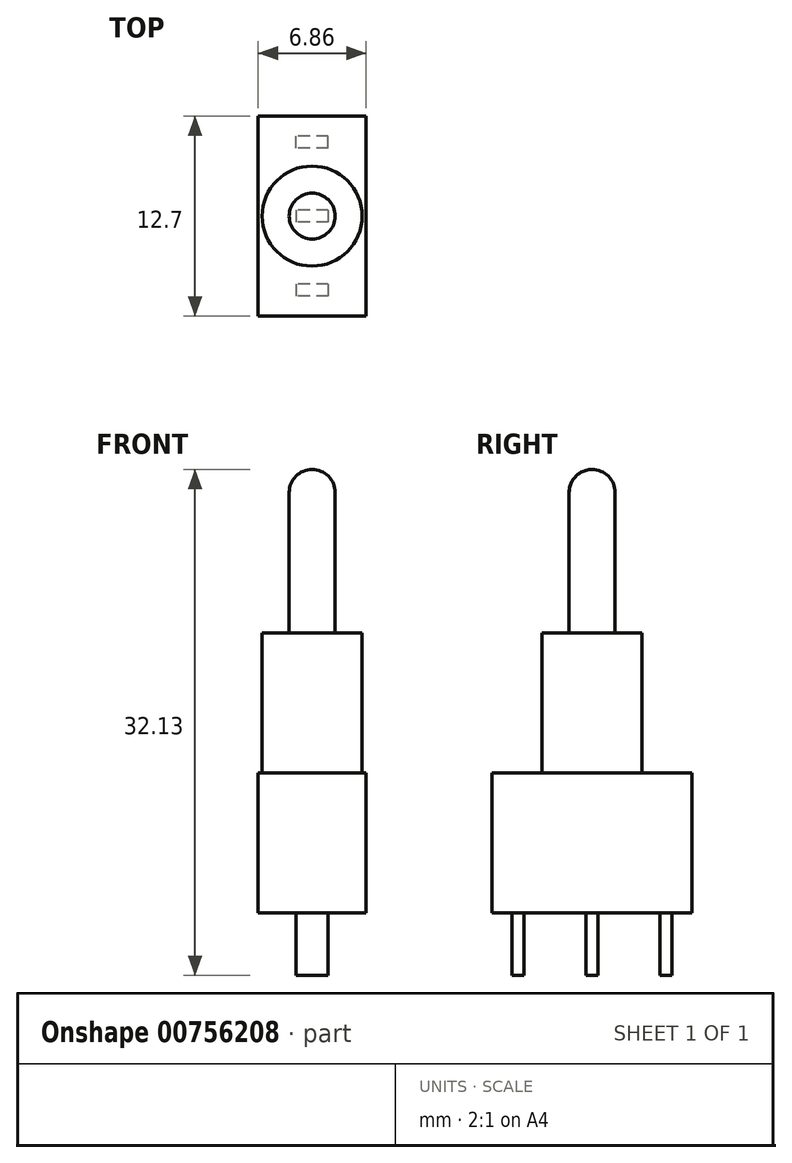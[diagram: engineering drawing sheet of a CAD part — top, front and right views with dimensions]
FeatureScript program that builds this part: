
annotation { "Feature Type Name" : "Feature", "Feature Type Description" : "" }
export const myFeature = defineFeature(function(context is Context, id is Id, definition is map)
    precondition{}
    {
        {
            var Q0;
            Q0=qCreatedBy(makeId("Top.planeOp"),FACE);
            var sketch = newSketch(context, id + "F0", { "sketchPlane" : qUnion([Q0])});
            skLineSegment(sketch, "E0.bottom", {"start": v(-3.43, 6.35) * mm, "end": v(3.43, 6.35) * mm});
            skLineSegment(sketch, "E0.top", {"start": v(-3.43, -6.35) * mm, "end": v(3.43, -6.35) * mm});
            skLineSegment(sketch, "E0.left", {"start": v(-3.43, 6.35) * mm, "end": v(-3.43, -6.35) * mm});
            skLineSegment(sketch, "E0.right", {"start": v(3.43, 6.35) * mm, "end": v(3.43, -6.35) * mm});
            skPoint(sketch, "E0.middle", {"position": v(0, 0) * mm});
            skSolve(sketch);
        }
        {
            var Q0;
            Q0 = qSketchRegion(id + "F0", true);
            extrude(context, id + "F1", {"entities" : qUnion([Q0]), "endBound" : BoundingType.SYMMETRIC, "depth" : 8.9 * mm, "offsetDistance" : 25 * mm});
        }
        {
            var Q0;
            Q0=makeQuery(id+"F1.opExtrude","CAP_FACE",FACE,{"disambiguationData":[OSD([sQuery(id+"F0.wireOp",EDGE,"E0.bottom"),sQuery(id+"F0.wireOp",EDGE,"E0.top"),sQuery(id+"F0.wireOp",EDGE,"E0.left"),sQuery(id+"F0.wireOp",EDGE,"E0.right")])],"isStart":false});
            var sketch = newSketch(context, id + "F2", { "sketchPlane" : qUnion([Q0])});
            skCircle(sketch, "E1", {"center": v(0, 0) * mm, "radius": 3.18 * mm});
            skSolve(sketch);
        }
        {
            var Q0;
            Q0 = qSketchRegion(id + "F2", true);
            extrude(context, id + "F3", {"entities" : qUnion([Q0]), "operationType" : NewBodyOperationType.ADD, "depth" : 8.9 * mm, "offsetDistance" : 25 * mm});
        }
        {
            var Q0;
            Q0=makeQuery(id+"F1.opExtrude","CAP_FACE",FACE,{"disambiguationData":[OSD([sQuery(id+"F0.wireOp",EDGE,"E0.bottom"),sQuery(id+"F0.wireOp",EDGE,"E0.top"),sQuery(id+"F0.wireOp",EDGE,"E0.left"),sQuery(id+"F0.wireOp",EDGE,"E0.right")])],"isStart":true});
            var sketch = newSketch(context, id + "F4", { "sketchPlane" : qUnion([Q0])});
            skLineSegment(sketch, "E2.bottom", {"start": v(1.01, -0.37) * mm, "end": v(-1.01, -0.38) * mm});
            skLineSegment(sketch, "E2.top", {"start": v(1.01, 0.38) * mm, "end": v(-1.01, 0.37) * mm});
            skLineSegment(sketch, "E2.left", {"start": v(1.01, -0.37) * mm, "end": v(1.01, 0.38) * mm});
            skLineSegment(sketch, "E2.right", {"start": v(-1.01, -0.38) * mm, "end": v(-1.01, 0.37) * mm});
            skPoint(sketch, "E2.middle", {"position": v(0, 0) * mm});
            skLineSegment(sketch, "E3.bottom", {"start": v(1.01, -4.32) * mm, "end": v(-1.01, -4.32) * mm});
            skLineSegment(sketch, "E3.top", {"start": v(1.01, -5.08) * mm, "end": v(-1.01, -5.08) * mm});
            skLineSegment(sketch, "E3.left", {"start": v(1.01, -4.32) * mm, "end": v(1.01, -5.08) * mm});
            skLineSegment(sketch, "E3.right", {"start": v(-1.01, -4.32) * mm, "end": v(-1.01, -5.08) * mm});
            skPoint(sketch, "E3.middle", {"position": v(0, -4.7) * mm});
            skLineSegment(sketch, "E4", {"start": v(3.43, 0) * mm, "end": v(-3.43, 0) * mm, "construction": true});
            skLineSegment(sketch, "E5.MirrorCS", {"start": v(1.01, 4.32) * mm, "end": v(-1.01, 4.32) * mm});
            skLineSegment(sketch, "E6.MirrorCS", {"start": v(1.01, 4.32) * mm, "end": v(1.01, 5.08) * mm});
            skLineSegment(sketch, "E7.MirrorCS", {"start": v(1.01, 5.08) * mm, "end": v(-1.01, 5.08) * mm});
            skLineSegment(sketch, "E8.MirrorCS", {"start": v(-1.01, 4.32) * mm, "end": v(-1.01, 5.08) * mm});
            skSolve(sketch);
        }
        {
            var Q0;
            Q0 = qSketchRegion(id + "F4", true);
            extrude(context, id + "F5", {"entities" : qUnion([Q0]), "operationType" : NewBodyOperationType.ADD, "depth" : 3.96 * mm, "offsetDistance" : 25 * mm});
        }
        {
            var Q0;
            Q0=qCreatedBy(makeId("Right.planeOp"),FACE);
            var sketch = newSketch(context, id + "F6", { "sketchPlane" : qUnion([Q0])});
            skLineSegment(sketch, "E9.0.0", {"start": v(-3.18, 13.33) * mm, "end": v(3.18, 13.33) * mm, "construction": true});
            skLineSegment(sketch, "E10", {"start": v(0, 13.33) * mm, "end": v(0, 17.8) * mm, "construction": true});
            skLineSegment(sketch, "E11.bottom", {"start": v(-1.46, 13.33) * mm, "end": v(1.46, 13.33) * mm});
            skLineSegment(sketch, "E11.top", {"start": v(-1.46, 22.28) * mm, "end": v(1.46, 22.28) * mm, "construction": true});
            skLineSegment(sketch, "E11.left", {"start": v(-1.46, 13.33) * mm, "end": v(-1.46, 22.27) * mm});
            skLineSegment(sketch, "E11.right", {"start": v(1.46, 13.33) * mm, "end": v(1.46, 22.28) * mm});
            skPoint(sketch, "E11.middle", {"position": v(0, 17.8) * mm});
            skArc(sketch, "E12", {"start": v(1.46, 22.28) * mm, "mid": v(0, 23.74) * mm, "end": v(-1.46, 22.27) * mm});
            skLineSegment(sketch, "E13", {"start": v(0, 23.74) * mm, "end": v(0, 13.33) * mm});
            skSolve(sketch);
        }
        {
            var Q0;
            {var subQ0=sQuery(id+"F6.wireOp",EDGE,"E11.left");Q0=makeQuery(id+"F6.imprint","IMPRINT",FACE,{"disambiguationData":[TD([[makeQuery(id+"F6.imprint","IMPRINT",EDGE,{"derivedFrom":subQ0}),-1.0]])]});}
            var Q1;
            Q1=sQuery(id+"F6.wireOp",EDGE,"E13");
            revolve(context, id + "F7", {"operationType" : NewBodyOperationType.ADD, "surfaceOperationType" : NewSurfaceOperationType.NEW, "entities" : qUnion([Q0]), "axis" : qUnion([Q1]), "revolveType" : RevolveType.FULL});
        }
    });
